# Revit family: Water_Softening_Systems-Commercial-Simplex-WATTS-Locksmith-CLS_Series
name_source: partatom
category: Pipe Accessories
units: mm (PartAtom-declared; Revit-internal decimal feet)

## family parameters
Always vertical = No
Cut with Voids When Loaded = No
OmniClass Number = 23.65.50.11.11.14
OmniClass Title = Water Softeners
Part Type = Normal
Round Connector Dimension = Use Diameter
Shared = Yes
Work Plane-Based = Yes

## types (13) — shared parameters
Assembly Code = D2090600
Brine Tank Material = Plastic-Watts-Polyethylene-Black
Country = United States
Default Elevation = 0"
Description = LOCKSMITH™ Series CLS Softeners for Hardness Reduction with Watts Exclusive Valve Controller, Pipe Size 1.5 - 2 IN
Drop PSI = 15/25
Electrical Requirement = 120V (60Hz)
Flow Rate = up to 119 gpm
Free Chlorine = 1mg/L
Hardness (Maximum) = Depends on customers acceptable hardness leakage level.
IAPMO Compliance = Control Valve - Certified to NSF/ANSI Std. 61 and 372; Ion Exchange Resin - Certified to NSF/ANSI Std. 61 and 372; Mineral Tank - Certified to NSF/ANSI Std. 44 or 61
Installation Instruction Link = https://www.watts.com
Iron = 1mg/L
Manufacturer = WATTS
Manufacturer Product Line = Backwashing Systems
Material = Plastic-Watts-Fibreglass
Mineral Tank Material = Plastic-Watts-Fibreglass
Oil and H2S = None Allowed
Price = Prices may vary. Please consult Manufacturer Representative for most up-to-date price list.
Product Documentation Link = https://www.watts.com
Product Page URL = https://www.watts.com
Region = North America
Temperature Range = 34 - 110°F (1 - 43°C)
Total Dissolved Solids = Must be below 750 mg/l for the softener to produce less than 1 grain per gallon soft water
Turbidity = Less than 5.0 NTU
URL = https://www.watts.com
Valve Material = Metal-Watts-Brass
Water Pressure = 25 psi to 125 psi (171 kPa to 8.5 bar
distance = 5/16"
pH = 6 to 10

## per-type parameters (varying)
- M4410L: A and B=53 1/4"; Backwash Flow Rate=4; Brine Tank Radius=9"; C=61"; Connection Radius=3/4"; Connection Size=1 1/2"; D=12"; E=16 3/4"; F=18"; FT3 Resin=3; G=40"; Gravel=30 lbs.; Inlet Connection Description=1 1/2" Inlet Supply Connection; LBS. Salt Per Regeneration=12-30 lbs.; Masking Radius=6"; Mineral Tank Height=52"; Mineral Tank Radius=6"; Mineral Tank Size Width=12"; Order Code:=68110950; Outlet Connection Description=1 1/2" Outlet Supply Connection; Salt Fill=400; Service Flow Rate=25 gpm/40 gpm; Shipping Weight=210 lbs. (95 kg.); Softening  (Min - Max)=40K-60K; Space Required (D X W X H)=24" x 44" 75"; Type Comments=2 Cubic Foot 1 1/2" Simplex Softener with Flow Meter
- M4414L: A and B=68 1/4"; Backwash Flow Rate=5; Brine Tank Radius=9"; C=73 5/8"; Connection Radius=3/4"; Connection Size=1 1/2"; D=14"; E=17 3/4"; F=18"; FT3 Resin=3; G=40"; Gravel=60 lbs.; Inlet Connection Description=1 1/2" Inlet Supply Connection; LBS. Salt Per Regeneration=18-45 lbs.; Masking Radius=7"; Mineral Tank Height=65"; Mineral Tank Radius=7"; Mineral Tank Size Width=14"; Order Code:=68110952; Outlet Connection Description=1 1/2" Outlet Supply Connection; Salt Fill=400; Service Flow Rate=35 gpm/55 gpm; Shipping Weight=240 lbs. (109 kg.); Softening  (Min - Max)=60K-90K; Space Required (D X W X H)=24" x 44" 75"; Type Comments=3 Cubic Foot 1 1/2" Simplex Softener with Flow Meter
- M4418L: A and B=68 1/4"; Backwash Flow Rate=7; Brine Tank Radius=9"; C=73 5/8"; Connection Radius=3/4"; Connection Size=1 1/2"; D=16"; E=18 3/4"; F=18"; FT3 Resin=4; G=40"; Gravel=80 lbs.; Inlet Connection Description=1 1/2" Inlet Supply Connection; LBS. Salt Per Regeneration=24-60 lbs.; Masking Radius=8"; Mineral Tank Height=65"; Mineral Tank Radius=8"; Mineral Tank Size Width=16"; Order Code:=68110954; Outlet Connection Description=1 1/2" Outlet Supply Connection; Salt Fill=400; Service Flow Rate=57 gpm/65 gpm; Shipping Weight=320 lbs. (145 kg.); Softening  (Min - Max)=80K-120K; Space Required (D X W X H)=24" x 44" 75"; Type Comments=4 Cubic Foot 1 1/2" Simplex Softener with Flow Meter
- M4422L: A and B=68 1/4"; Backwash Flow Rate=11; Brine Tank Radius=12"; C=73 5/8"; Connection Radius=3/4"; Connection Size=1 1/2"; D=18"; E=20 3/4"; F=24"; FT3 Resin=5; G=41"; Gravel=100 lbs.; Inlet Connection Description=1 1/2" Inlet Supply Connection; LBS. Salt Per Regeneration=30-75 lbs.; Masking Radius=9"; Mineral Tank Height=65"; Mineral Tank Radius=9"; Mineral Tank Size Width=18"; Order Code:=68110956; Outlet Connection Description=1 1/2" Outlet Supply Connection; Salt Fill=600; Service Flow Rate=60 gpm/ 77 gpm; Shipping Weight=380 lbs. (172 kg.); Softening  (Min - Max)=100K-150K; Space Required (D X W X H)=24" x 50" x 87"; Type Comments=5 Cubic Foot 1 1/2" Simplex Softener with Flow Meter
- M4426L: A and B=65 1/4"; Backwash Flow Rate=13; Brine Tank Radius=12"; C=70 5/8"; Connection Radius=3/4"; Connection Size=1 1/2"; D=21"; E=21 3/4"; F=24"; FT3 Resin=7; G=41"; Gravel=100 lbs.; Inlet Connection Description=1 1/2" Inlet Supply Connection; LBS. Salt Per Regeneration=42-105 lbs.; Masking Radius=10 1/2"; Mineral Tank Height=62"; Mineral Tank Radius=10 1/2"; Mineral Tank Size Width=21"; Order Code:=68110961; Outlet Connection Description=1 1/2" Outlet Supply Connection; Salt Fill=800; Service Flow Rate=74 gpm/ 97 gpm; Shipping Weight=585 lbs. (265 kg.); Softening  (Min - Max)=140K-210K; Space Required (D X W X H)=24" x 52" x 84"; Type Comments=7 Cubic Foot 1 1/2" Simplex Softener with Flow Meter
- M4430L: A and B=75 1/4"; Backwash Flow Rate=15; Brine Tank Radius=15"; C=80 5/8"; Connection Radius=3/4"; Connection Size=1 1/2"; D=24"; E=24 1/4"; F=30"; FT3 Resin=10; G=50"; Gravel=200 lbs.; Inlet Connection Description=1 1/2" Inlet Supply Connection; LBS. Salt Per Regeneration=60-150 lbs.; Masking Radius=12"; Mineral Tank Height=72"; Mineral Tank Radius=12"; Mineral Tank Size Width=24"; Order Code:=68110966; Outlet Connection Description=1 1/2" Outlet Supply Connection; Salt Fill=1400; Service Flow Rate=80 gpm/ 100 gpm; Shipping Weight=710 lbs. (322 kg.); Softening  (Min - Max)=200K-300K; Space Required (D X W X H)=30" x 69" x 96"; Type Comments=10 Cubic Foot 1 1/2" Simplex Softener with Flow Meter
- M4543L: A and B=68 1/2"; Backwash Flow Rate=5; Brine Tank Radius=9"; C=74 1/4"; Connection Radius=1"; Connection Size=2"; D=14"; E=17 3/4"; F=18"; FT3 Resin=3; G=40"; Gravel=60 lbs.; Inlet Connection Description=2" Inlet Supply Connection; LBS. Salt Per Regeneration=18-45 lbs.; Masking Radius=7"; Mineral Tank Height=65"; Mineral Tank Radius=7"; Mineral Tank Size Width=14"; Order Code:=68110971; Outlet Connection Description=2" Outlet Supply Connection; Salt Fill=400; Service Flow Rate=39 gpm/55 gpm; Shipping Weight=265 lbs. (120 kg.); Softening  (Min - Max)=60K-90K; Space Required (D X W X H)=24" x 44" x 87"; Type Comments=3 Cubic Foot 2" Simplex Softener with Flow Meter
- M4547L: A and B=68 1/2"; Backwash Flow Rate=7; Brine Tank Radius=9"; C=74 1/4"; Connection Radius=1"; Connection Size=2"; D=16"; E=18 1/2"; F=18"; FT3 Resin=4; G=40"; Gravel=80 lbs.; Inlet Connection Description=2" Inlet Supply Connection; LBS. Salt Per Regeneration=24-60 lbs.; Masking Radius=8"; Mineral Tank Height=65"; Mineral Tank Radius=8"; Mineral Tank Size Width=16"; Order Code:=68110973; Outlet Connection Description=2" Outlet Supply Connection; Salt Fill=400; Service Flow Rate=47 gpm/60 gpm; Shipping Weight=350 lbs. (159 kg.); Softening  (Min - Max)=80K-120K; Space Required (D X W X H)=24" x 44" x 87"; Type Comments=4 Cubic Foot 2" Simplex Softener with Flow Meter
- M4548L: A and B=68 1/2"; Backwash Flow Rate=10; Brine Tank Radius=12"; C=74 1/4"; Connection Radius=1"; Connection Size=2"; D=18"; E=20 1/2"; F=24"; FT3 Resin=5; G=41"; Gravel=100 lbs.; Inlet Connection Description=2" Inlet Supply Connection; LBS. Salt Per Regeneration=30-75 lbs.; Masking Radius=9"; Mineral Tank Height=65"; Mineral Tank Radius=9"; Mineral Tank Size Width=18"; Order Code:=68110975; Outlet Connection Description=2" Outlet Supply Connection; Salt Fill=600; Service Flow Rate=53 gpm/69 gpm; Shipping Weight=400 lbs. (181 kg.); Softening  (Min - Max)=100K-150K; Space Required (D X W X H)=24" x 48" x 89"; Type Comments=5 Cubic Foot 2" Simplex Softener with Flow Meter
- M4552L: A and B=65 1/2"; Backwash Flow Rate=13; Brine Tank Radius=12"; C=73"; Connection Radius=1"; Connection Size=2"; D=21"; E=21 1/4"; F=24"; FT3 Resin=7; G=41"; Gravel=100 lbs.; Inlet Connection Description=2" Inlet Supply Connection; LBS. Salt Per Regeneration=42-105 lbs.; Masking Radius=10 1/2"; Mineral Tank Height=62"; Mineral Tank Radius=10 1/2"; Mineral Tank Size Width=21"; Order Code:=68110980; Outlet Connection Description=2" Outlet Supply Connection; Salt Fill=600; Service Flow Rate=66 gpm/85 gpm; Shipping Weight=600 lbs. (272kg.); Softening  (Min - Max)=140K-210K; Space Required (D X W X H)=24" x 52" x 89"; Type Comments=7 Cubic Foot 2" Simplex Softener with Flow Meter
- M4558L: A and B=75 1/2"; Backwash Flow Rate=15; Brine Tank Radius=15"; C=83"; Connection Radius=1"; Connection Size=2"; D=24"; E=24 1/4"; F=30"; FT3 Resin=10; G=50"; Gravel=200 lbs.; Inlet Connection Description=2" Inlet Supply Connection; LBS. Salt Per Regeneration=60-150 lbs.; Masking Radius=12"; Mineral Tank Height=72"; Mineral Tank Radius=12"; Mineral Tank Size Width=24"; Order Code:=68110985; Outlet Connection Description=2" Outlet Supply Connection; Salt Fill=1400; Service Flow Rate=73gpm/94 gpm; Shipping Weight=710 lbs. (322kg.); Softening  (Min - Max)=200K-300K; Space Required (D X W X H)=30" x 69" x 96"; Type Comments=10 Cubic Foot 2" Simplex Softener with Flow Meter
- M4559L: A and B=75 1/2"; Backwash Flow Rate=25; Brine Tank Radius=19 1/2"; C=83"; Connection Radius=1"; Connection Size=2"; D=30"; E=30 1/4"; F=39"; FT3 Resin=15; G=48"; Gravel=400 lbs.; Inlet Connection Description=2" Inlet Supply Connection; LBS. Salt Per Regeneration=90-225 lbs.; Masking Radius=15"; Mineral Tank Height=72"; Mineral Tank Radius=15"; Mineral Tank Size Width=30"; Order Code:=68110991; Outlet Connection Description=2" Outlet Supply Connection; Salt Fill=2200; Service Flow Rate=84gpm/109 gpm; Shipping Weight=1160 lbs. (526kg.); Softening  (Min - Max)=300K-450K; Space Required (D X W X H)=39" x 75" x 106"; Type Comments=15 Cubic Foot 2" Simplex Softener with Flow Meter
- M4560L: A and B=75 1/2"; Backwash Flow Rate=35; Brine Tank Radius=19 1/2"; C=83"; Connection Radius=1"; Connection Size=2"; D=36"; E=36 1/4"; F=39"; FT3 Resin=20; G=48"; Gravel=500 lbs.; Inlet Connection Description=2" Inlet Supply Connection; LBS. Salt Per Regeneration=120-300 lbs.; Masking Radius=18"; Mineral Tank Height=72"; Mineral Tank Radius=18"; Mineral Tank Size Width=36"; Order Code:=68110996; Outlet Connection Description=2" Outlet Supply Connection; Salt Fill=2200; Service Flow Rate=93gpm/119 gpm; Shipping Weight=1560 lbs. (707kg.); Softening  (Min - Max)=400K-600K; Space Required (D X W X H)=39" x 81" x 107"; Type Comments=20 Cubic Foot 2" Simplex Softener with Flow Meter

note: column(s) folded — value = type name in every type: Model

## geometry (parser evidence)
native form markers: Sweep x4
no freeform markers — native parametric forms only
